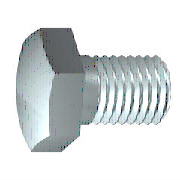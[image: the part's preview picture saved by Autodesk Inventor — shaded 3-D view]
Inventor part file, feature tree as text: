
AUTODESK INVENTOR PART (.ipt)
format: ipt  version: 2013 (Build 170138000, 138)  size: 185,856 bytes
history: native  units: mm (DEFAULTED — no unit token found)
features: sketch x2, extrude x1, chamfer x1, plane x1
ambient origin geometry x7: Origin, YZ Plane, XZ Plane, X Axis, Y Axis, Z Axis, Center Point
bodies: Solid1 (feature_tree), Body (feature_tree)
feature tree (5):
  extrude  "Head"  TaperAngle=90.0deg  [1 undecoded]
  chamfer  "Chamfer1"  [1 undecoded]
  plane  "Work Plane1"
  sketch  "Sketch1"  dims[d2=8.0mm d12=90.0deg]
  sketch  "Sketch2"  dims[d3=5.68mm d4=0.0mm d21=90.0deg d6=0.766813mm d7=0.766912mm d8=0.0mm d11=13.0mm d15=22.0mm d16=0.0mm d55=45.0deg d58=0.0mm d59=30.0mm d65=13.0mm d67=30.0deg d68=15.6mm d69=5.68mm d71=0.1mm d73=0.0mm]
note: 2 required parameter values undecoded (feature->parameter linkage not recoverable at this tier; creation-order binding heuristic only, values carry confidence <= 0.55)
